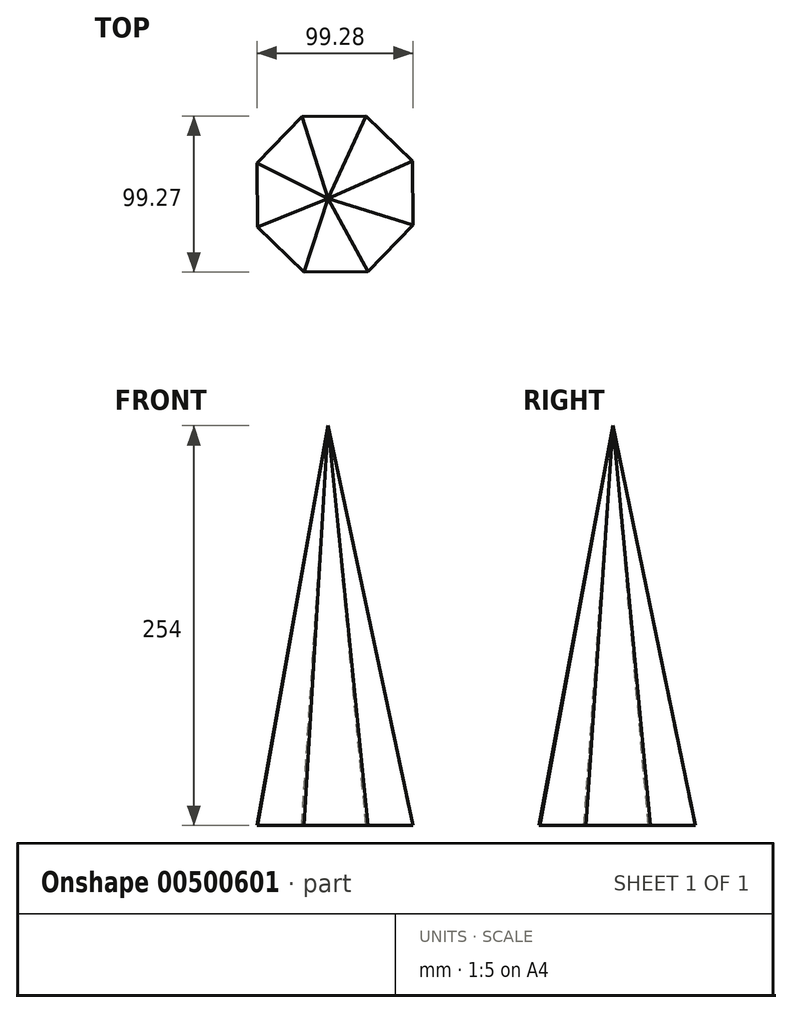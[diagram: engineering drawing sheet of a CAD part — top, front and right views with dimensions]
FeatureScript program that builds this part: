
annotation { "Feature Type Name" : "Feature", "Feature Type Description" : "" }
export const myFeature = defineFeature(function(context is Context, id is Id, definition is map)
    precondition{}
    {
        {
            var Q0;
            Q0=qCreatedBy(makeId("Top.planeOp"),FACE);
            var sketch = newSketch(context, id + "F0", { "sketchPlane" : qUnion([Q0])});
            skCircle(sketch, "E0.cCircle", {"center": v(0, 15.5) * mm, "radius": 53.45 * mm, "construction": true});
            skLineSegment(sketch, "E0.0", {"start": v(-21.08, 64.62) * mm, "end": v(19.82, 65.14) * mm});
            skLineSegment(sketch, "E0.1", {"start": v(19.82, 65.14) * mm, "end": v(49.11, 36.6) * mm});
            skLineSegment(sketch, "E0.2", {"start": v(49.11, 36.6) * mm, "end": v(49.64, -4.31) * mm});
            skLineSegment(sketch, "E0.3", {"start": v(49.64, -4.31) * mm, "end": v(21.08, -33.6) * mm});
            skLineSegment(sketch, "E0.4", {"start": v(21.08, -33.6) * mm, "end": v(-19.82, -34.13) * mm});
            skLineSegment(sketch, "E0.5", {"start": v(-19.82, -34.13) * mm, "end": v(-49.11, -5.58) * mm});
            skLineSegment(sketch, "E0.6", {"start": v(-49.11, -5.58) * mm, "end": v(-49.64, 35.33) * mm});
            skLineSegment(sketch, "E0.7", {"start": v(-49.64, 35.33) * mm, "end": v(-21.08, 64.62) * mm});
            skSolve(sketch);
        }
        {
            var Q0;
            Q0=qCreatedBy(makeId("Top.planeOp"),FACE);
            cPlane(context, id + "F1", {"entities" : qUnion([Q0]), "cplaneType" : CPlaneType.OFFSET, "offset" : 254 * mm, "width" : 152.4 * mm, "height" : 152.4 * mm});
        }
        {
            var Q0;
            Q0=qCreatedBy(id+"F1.planeOp",FACE);
            var sketch = newSketch(context, id + "F2", { "sketchPlane" : qUnion([Q0])});
            skPoint(sketch, "E1", {"position": v(-4.37, 12.68) * mm});
            skSolve(sketch);
        }
        {
            var Q0;
            Q0=makeQuery(id+"F0.imprint","IMPRINT",FACE,{"disambiguationData":[TD([[makeQuery(id+"F0.imprint","IMPRINT",EDGE,{"derivedFrom":sQuery(id+"F0.wireOp",EDGE,"E0.0")}),-1.0]])]});
            var Q1;
            Q1=sQuery(id+"F2.wireOp",VERTEX,"E1");
            loft(context, id + "F3", {"sheetProfilesArray" : [{ "sheetProfileEntities" : qUnion([Q0]) }, { "sheetProfileEntities" : qUnion([Q1]) }]});
        }
    });
